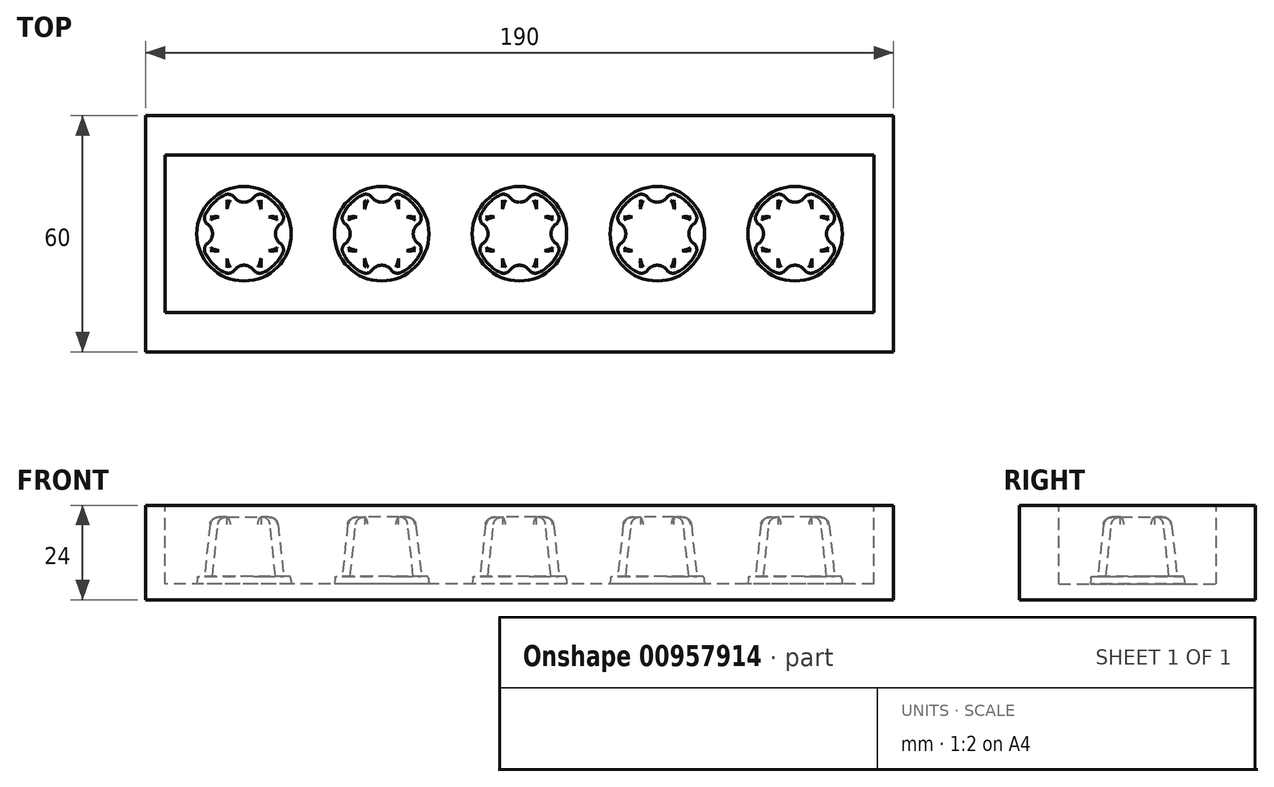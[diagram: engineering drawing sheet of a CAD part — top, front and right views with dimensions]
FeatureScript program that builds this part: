
annotation { "Feature Type Name" : "Feature", "Feature Type Description" : "" }
export const myFeature = defineFeature(function(context is Context, id is Id, definition is map)
    precondition{}
    {
        {
            var Q0;
            Q0=qCreatedBy(makeId("Top.planeOp"),FACE);
            var sketch = newSketch(context, id + "F0", { "sketchPlane" : qUnion([Q0])});
            skLineSegment(sketch, "E0.bottom", {"start": v(0, 0) * mm, "end": v(190, 0) * mm});
            skLineSegment(sketch, "E0.top", {"start": v(0, -60) * mm, "end": v(190, -60) * mm});
            skLineSegment(sketch, "E0.left", {"start": v(0, 0) * mm, "end": v(0, -60) * mm});
            skLineSegment(sketch, "E0.right", {"start": v(190, 0) * mm, "end": v(190, -60) * mm});
            skSolve(sketch);
        }
        {
            var Q0;
            Q0=makeQuery(id+"F0.imprint","IMPRINT",FACE,{"disambiguationData":[TD([[makeQuery(id+"F0.imprint","IMPRINT",EDGE,{"derivedFrom":sQuery(id+"F0.wireOp",EDGE,"E0.bottom")}),-1.0]])]});
            extrude(context, id + "F1", {"entities" : qUnion([Q0]), "depth" : 24 * mm, "offsetDistance" : 25 * mm});
        }
        {
            var Q0;
            Q0=makeQuery(id+"F1.opExtrude","CAP_FACE",FACE,{"disambiguationData":[OSD([sQuery(id+"F0.wireOp",EDGE,"E0.bottom"),sQuery(id+"F0.wireOp",EDGE,"E0.top"),sQuery(id+"F0.wireOp",EDGE,"E0.left"),sQuery(id+"F0.wireOp",EDGE,"E0.right")])],"isStart":false});
            var sketch = newSketch(context, id + "F2", { "sketchPlane" : qUnion([Q0])});
            skLineSegment(sketch, "E1.bottom", {"start": v(185, -50) * mm, "end": v(5, -50) * mm});
            skLineSegment(sketch, "E1.top", {"start": v(185, -10) * mm, "end": v(5, -10) * mm});
            skLineSegment(sketch, "E1.left", {"start": v(185, -50) * mm, "end": v(185, -10) * mm});
            skLineSegment(sketch, "E1.right", {"start": v(5, -50) * mm, "end": v(5, -10) * mm});
            skPoint(sketch, "E1.middle", {"position": v(95, -30) * mm});
            skPoint(sketch, "E1.middle.positionSnap0", {"position": v(0, -30) * mm});
            skPoint(sketch, "E1.middle.positionSnap1", {"position": v(95, 0) * mm});
            skPoint(sketch, "E1.centerSnap0", {"position": v(0, -30) * mm});
            skPoint(sketch, "E1.centerSnap1", {"position": v(95, 0) * mm});
            skSolve(sketch);
        }
        {
            var Q0;
            Q0=makeQuery(id+"F2.imprint","IMPRINT",FACE,{"disambiguationData":[TD([[makeQuery(id+"F2.imprint","IMPRINT",EDGE,{"derivedFrom":sQuery(id+"F2.wireOp",EDGE,"E1.bottom")}),-1.0]])]});
            extrude(context, id + "F3", {"entities" : qUnion([Q0]), "operationType" : NewBodyOperationType.REMOVE, "oppositeDirection" : true, "depth" : 20 * mm, "offsetDistance" : 25 * mm});
        }
        {
            var Q0;
            Q0=makeQuery(id+"F3.boolean.opBoolean","COPY",FACE,{"derivedFrom":makeQuery(id+"F3.opExtrude","CAP_FACE",FACE,{"disambiguationData":[OSD([sQuery(id+"F2.wireOp",EDGE,"E1.bottom"),sQuery(id+"F2.wireOp",EDGE,"E1.top"),sQuery(id+"F2.wireOp",EDGE,"E1.left"),sQuery(id+"F2.wireOp",EDGE,"E1.right")])],"isStart":false})});
            var sketch = newSketch(context, id + "F4", { "sketchPlane" : qUnion([Q0])});
            skLineSegment(sketch, "E2", {"start": v(5, -30) * mm, "end": v(185, -30) * mm, "construction": true});
            skCircle(sketch, "E3", {"center": v(25, -30) * mm, "radius": 12 * mm});
            skCircle(sketch, "E4.1.0.0", {"center": v(60, -30) * mm, "radius": 12 * mm});
            skCircle(sketch, "E4.2.0.0", {"center": v(95, -30) * mm, "radius": 12 * mm});
            skCircle(sketch, "E4.3.0.0", {"center": v(130, -30) * mm, "radius": 12 * mm});
            skCircle(sketch, "E4.4.0.0", {"center": v(165, -30) * mm, "radius": 12 * mm});
            skLineSegment(sketch, "E4.direction1", {"start": v(25, -30) * mm, "end": v(60, -30) * mm, "construction": true});
            skSolve(sketch);
        }
        {
            var Q0;
            Q0=makeQuery(id+"F4.imprint","IMPRINT",FACE,{"disambiguationData":[TD([[makeQuery(id+"F4.imprint","IMPRINT",EDGE,{"derivedFrom":sQuery(id+"F4.wireOp",EDGE,"E3")}),1.0]])]});
            var Q1;
            Q1=makeQuery(id+"F4.imprint","IMPRINT",FACE,{"disambiguationData":[TD([[makeQuery(id+"F4.imprint","IMPRINT",EDGE,{"derivedFrom":sQuery(id+"F4.wireOp",EDGE,"E4.1.0.0")}),1.0]])]});
            var Q2;
            Q2=makeQuery(id+"F4.imprint","IMPRINT",FACE,{"disambiguationData":[TD([[makeQuery(id+"F4.imprint","IMPRINT",EDGE,{"derivedFrom":sQuery(id+"F4.wireOp",EDGE,"E4.2.0.0")}),1.0]])]});
            var Q3;
            Q3=makeQuery(id+"F4.imprint","IMPRINT",FACE,{"disambiguationData":[TD([[makeQuery(id+"F4.imprint","IMPRINT",EDGE,{"derivedFrom":sQuery(id+"F4.wireOp",EDGE,"E4.3.0.0")}),1.0]])]});
            var Q4;
            Q4=makeQuery(id+"F4.imprint","IMPRINT",FACE,{"disambiguationData":[TD([[makeQuery(id+"F4.imprint","IMPRINT",EDGE,{"derivedFrom":sQuery(id+"F4.wireOp",EDGE,"E4.4.0.0")}),1.0]])]});
            extrude(context, id + "F5", {"entities" : qUnion([Q0, Q1, Q2, Q3, Q4]), "operationType" : NewBodyOperationType.ADD, "depth" : 2 * mm, "offsetDistance" : 25 * mm, "hasDraft" : true, "draftAngle" : 6 * degree, "draftPullDirection" : true});
        }
        {
            var Q0;
            Q0=makeQuery(id+"F5.opExtrude","CAP_FACE",FACE,{"disambiguationData":[OSD([sQuery(id+"F4.wireOp",EDGE,"E3")])],"isStart":false});
            var sketch = newSketch(context, id + "F6", { "sketchPlane" : qUnion([Q0])});
            skArc(sketch, "E5", {"start": v(20.07, -20.17) * mm, "mid": v(17.22, -22.22) * mm, "end": v(15.17, -25.07) * mm});
            skArc(sketch, "E6", {"start": v(22.58, -20.77) * mm, "mid": v(25, -22) * mm, "end": v(27.42, -20.77) * mm});
            skArc(sketch, "E7", {"start": v(34.23, -27.58) * mm, "mid": v(33, -30) * mm, "end": v(34.23, -32.42) * mm});
            skArc(sketch, "E8", {"start": v(27.42, -39.23) * mm, "mid": v(25, -38) * mm, "end": v(22.58, -39.23) * mm});
            skArc(sketch, "E9", {"start": v(15.77, -32.42) * mm, "mid": v(17, -30) * mm, "end": v(15.77, -27.58) * mm});
            skArc(sketch, "E10.trimOffspring", {"start": v(34.83, -25.07) * mm, "mid": v(32.78, -22.22) * mm, "end": v(29.93, -20.17) * mm});
            skArc(sketch, "E11.trimOffspring", {"start": v(29.93, -39.83) * mm, "mid": v(32.78, -37.78) * mm, "end": v(34.83, -34.93) * mm});
            skArc(sketch, "E12.trimOffspring", {"start": v(15.17, -34.93) * mm, "mid": v(17.22, -37.78) * mm, "end": v(20.07, -39.83) * mm});
            skPoint(sketch, "E13.visualSharp", {"position": v(22.03, -19.4) * mm});
            skArc(sketch, "E13.filletArc", {"start": v(22.58, -20.77) * mm, "mid": v(21.44, -20.01) * mm, "end": v(20.07, -20.17) * mm});
            skPoint(sketch, "E14.visualSharp", {"position": v(27.97, -19.4) * mm});
            skArc(sketch, "E14.filletArc", {"start": v(29.93, -20.17) * mm, "mid": v(28.56, -20.01) * mm, "end": v(27.42, -20.77) * mm});
            skPoint(sketch, "E15.visualSharp", {"position": v(35.6, -27.03) * mm});
            skArc(sketch, "E15.filletArc", {"start": v(34.23, -27.58) * mm, "mid": v(34.99, -26.44) * mm, "end": v(34.83, -25.07) * mm});
            skPoint(sketch, "E16.visualSharp", {"position": v(35.6, -32.97) * mm});
            skArc(sketch, "E16.filletArc", {"start": v(34.83, -34.93) * mm, "mid": v(34.99, -33.56) * mm, "end": v(34.23, -32.42) * mm});
            skPoint(sketch, "E17.visualSharp", {"position": v(27.97, -40.6) * mm});
            skArc(sketch, "E17.filletArc", {"start": v(27.42, -39.23) * mm, "mid": v(28.56, -39.99) * mm, "end": v(29.93, -39.83) * mm});
            skPoint(sketch, "E18.visualSharp", {"position": v(22.03, -40.6) * mm});
            skArc(sketch, "E18.filletArc", {"start": v(20.07, -39.83) * mm, "mid": v(21.44, -39.99) * mm, "end": v(22.58, -39.23) * mm});
            skPoint(sketch, "E19.visualSharp", {"position": v(14.4, -32.97) * mm});
            skArc(sketch, "E19.filletArc", {"start": v(15.77, -32.42) * mm, "mid": v(15.01, -33.56) * mm, "end": v(15.17, -34.93) * mm});
            skPoint(sketch, "E20.visualSharp", {"position": v(14.4, -27.03) * mm});
            skArc(sketch, "E20.filletArc", {"start": v(15.17, -25.07) * mm, "mid": v(15.01, -26.44) * mm, "end": v(15.77, -27.58) * mm});
            skPoint(sketch, "E21.1.0.0", {"position": v(70.6, -32.97) * mm});
            skPoint(sketch, "E21.1.0.1", {"position": v(62.97, -19.4) * mm});
            skArc(sketch, "E21.1.0.2", {"start": v(50.77, -32.42) * mm, "mid": v(52, -30) * mm, "end": v(50.77, -27.58) * mm});
            skPoint(sketch, "E21.1.0.3", {"position": v(70.6, -27.03) * mm});
            skArc(sketch, "E21.1.0.4", {"start": v(64.93, -39.83) * mm, "mid": v(67.78, -37.78) * mm, "end": v(69.83, -34.93) * mm});
            skPoint(sketch, "E21.1.0.5", {"position": v(57.03, -40.6) * mm});
            skPoint(sketch, "E21.1.0.6", {"position": v(57.03, -19.4) * mm});
            skArc(sketch, "E21.1.0.7", {"start": v(62.42, -39.23) * mm, "mid": v(60, -38) * mm, "end": v(57.58, -39.23) * mm});
            skPoint(sketch, "E21.1.0.8", {"position": v(49.4, -32.97) * mm});
            skArc(sketch, "E21.1.0.9", {"start": v(57.58, -20.77) * mm, "mid": v(60, -22) * mm, "end": v(62.42, -20.77) * mm});
            skArc(sketch, "E21.1.0.10", {"start": v(55.07, -20.17) * mm, "mid": v(52.22, -22.22) * mm, "end": v(50.17, -25.07) * mm});
            skArc(sketch, "E21.1.0.11", {"start": v(69.23, -27.58) * mm, "mid": v(68, -30) * mm, "end": v(69.23, -32.42) * mm});
            skArc(sketch, "E21.1.0.12", {"start": v(50.17, -34.93) * mm, "mid": v(52.22, -37.78) * mm, "end": v(55.07, -39.83) * mm});
            skPoint(sketch, "E21.1.0.13", {"position": v(62.97, -40.6) * mm});
            skArc(sketch, "E21.1.0.14", {"start": v(69.83, -25.07) * mm, "mid": v(67.78, -22.22) * mm, "end": v(64.93, -20.17) * mm});
            skPoint(sketch, "E21.1.0.15", {"position": v(49.4, -27.03) * mm});
            skArc(sketch, "E21.1.0.16", {"start": v(62.42, -39.23) * mm, "mid": v(63.56, -39.99) * mm, "end": v(64.93, -39.83) * mm});
            skArc(sketch, "E21.1.0.17", {"start": v(50.77, -32.42) * mm, "mid": v(50.01, -33.56) * mm, "end": v(50.17, -34.93) * mm});
            skArc(sketch, "E21.1.0.18", {"start": v(69.83, -34.93) * mm, "mid": v(69.99, -33.56) * mm, "end": v(69.23, -32.42) * mm});
            skArc(sketch, "E21.1.0.19", {"start": v(69.23, -27.58) * mm, "mid": v(69.99, -26.44) * mm, "end": v(69.83, -25.07) * mm});
            skArc(sketch, "E21.1.0.20", {"start": v(57.58, -20.77) * mm, "mid": v(56.44, -20.01) * mm, "end": v(55.07, -20.17) * mm});
            skArc(sketch, "E21.1.0.21", {"start": v(55.07, -39.83) * mm, "mid": v(56.44, -39.99) * mm, "end": v(57.58, -39.23) * mm});
            skArc(sketch, "E21.1.0.22", {"start": v(64.93, -20.17) * mm, "mid": v(63.56, -20.01) * mm, "end": v(62.42, -20.77) * mm});
            skArc(sketch, "E21.1.0.23", {"start": v(50.17, -25.07) * mm, "mid": v(50.01, -26.44) * mm, "end": v(50.77, -27.58) * mm});
            skPoint(sketch, "E21.2.0.0", {"position": v(105.6, -32.97) * mm});
            skPoint(sketch, "E21.2.0.1", {"position": v(97.97, -19.4) * mm});
            skArc(sketch, "E21.2.0.2", {"start": v(85.77, -32.42) * mm, "mid": v(87, -30) * mm, "end": v(85.77, -27.58) * mm});
            skPoint(sketch, "E21.2.0.3", {"position": v(105.6, -27.03) * mm});
            skArc(sketch, "E21.2.0.4", {"start": v(99.93, -39.83) * mm, "mid": v(102.78, -37.78) * mm, "end": v(104.83, -34.93) * mm});
            skPoint(sketch, "E21.2.0.5", {"position": v(92.03, -40.6) * mm});
            skPoint(sketch, "E21.2.0.6", {"position": v(92.03, -19.4) * mm});
            skArc(sketch, "E21.2.0.7", {"start": v(97.42, -39.23) * mm, "mid": v(95, -38) * mm, "end": v(92.58, -39.23) * mm});
            skPoint(sketch, "E21.2.0.8", {"position": v(84.4, -32.97) * mm});
            skArc(sketch, "E21.2.0.9", {"start": v(92.58, -20.77) * mm, "mid": v(95, -22) * mm, "end": v(97.42, -20.77) * mm});
            skArc(sketch, "E21.2.0.10", {"start": v(90.07, -20.17) * mm, "mid": v(87.22, -22.22) * mm, "end": v(85.17, -25.07) * mm});
            skArc(sketch, "E21.2.0.11", {"start": v(104.23, -27.58) * mm, "mid": v(103, -30) * mm, "end": v(104.23, -32.42) * mm});
            skArc(sketch, "E21.2.0.12", {"start": v(85.17, -34.93) * mm, "mid": v(87.22, -37.78) * mm, "end": v(90.07, -39.83) * mm});
            skPoint(sketch, "E21.2.0.13", {"position": v(97.97, -40.6) * mm});
            skArc(sketch, "E21.2.0.14", {"start": v(104.83, -25.07) * mm, "mid": v(102.78, -22.22) * mm, "end": v(99.93, -20.17) * mm});
            skPoint(sketch, "E21.2.0.15", {"position": v(84.4, -27.03) * mm});
            skArc(sketch, "E21.2.0.16", {"start": v(97.42, -39.23) * mm, "mid": v(98.56, -39.99) * mm, "end": v(99.93, -39.83) * mm});
            skArc(sketch, "E21.2.0.17", {"start": v(85.77, -32.42) * mm, "mid": v(85.01, -33.56) * mm, "end": v(85.17, -34.93) * mm});
            skArc(sketch, "E21.2.0.18", {"start": v(104.83, -34.93) * mm, "mid": v(104.99, -33.56) * mm, "end": v(104.23, -32.42) * mm});
            skArc(sketch, "E21.2.0.19", {"start": v(104.23, -27.58) * mm, "mid": v(104.99, -26.44) * mm, "end": v(104.83, -25.07) * mm});
            skArc(sketch, "E21.2.0.20", {"start": v(92.58, -20.77) * mm, "mid": v(91.44, -20.01) * mm, "end": v(90.07, -20.17) * mm});
            skArc(sketch, "E21.2.0.21", {"start": v(90.07, -39.83) * mm, "mid": v(91.44, -39.99) * mm, "end": v(92.58, -39.23) * mm});
            skArc(sketch, "E21.2.0.22", {"start": v(99.93, -20.17) * mm, "mid": v(98.56, -20.01) * mm, "end": v(97.42, -20.77) * mm});
            skArc(sketch, "E21.2.0.23", {"start": v(85.17, -25.07) * mm, "mid": v(85.01, -26.44) * mm, "end": v(85.77, -27.58) * mm});
            skPoint(sketch, "E21.3.0.0", {"position": v(140.6, -32.97) * mm});
            skPoint(sketch, "E21.3.0.1", {"position": v(132.97, -19.4) * mm});
            skArc(sketch, "E21.3.0.2", {"start": v(120.77, -32.42) * mm, "mid": v(122, -30) * mm, "end": v(120.77, -27.58) * mm});
            skPoint(sketch, "E21.3.0.3", {"position": v(140.6, -27.03) * mm});
            skArc(sketch, "E21.3.0.4", {"start": v(134.93, -39.83) * mm, "mid": v(137.78, -37.78) * mm, "end": v(139.83, -34.93) * mm});
            skPoint(sketch, "E21.3.0.5", {"position": v(127.03, -40.6) * mm});
            skPoint(sketch, "E21.3.0.6", {"position": v(127.03, -19.4) * mm});
            skArc(sketch, "E21.3.0.7", {"start": v(132.42, -39.23) * mm, "mid": v(130, -38) * mm, "end": v(127.58, -39.23) * mm});
            skPoint(sketch, "E21.3.0.8", {"position": v(119.4, -32.97) * mm});
            skArc(sketch, "E21.3.0.9", {"start": v(127.58, -20.77) * mm, "mid": v(130, -22) * mm, "end": v(132.42, -20.77) * mm});
            skArc(sketch, "E21.3.0.10", {"start": v(125.07, -20.17) * mm, "mid": v(122.22, -22.22) * mm, "end": v(120.17, -25.07) * mm});
            skArc(sketch, "E21.3.0.11", {"start": v(139.23, -27.58) * mm, "mid": v(138, -30) * mm, "end": v(139.23, -32.42) * mm});
            skArc(sketch, "E21.3.0.12", {"start": v(120.17, -34.93) * mm, "mid": v(122.22, -37.78) * mm, "end": v(125.07, -39.83) * mm});
            skPoint(sketch, "E21.3.0.13", {"position": v(132.97, -40.6) * mm});
            skArc(sketch, "E21.3.0.14", {"start": v(139.83, -25.07) * mm, "mid": v(137.78, -22.22) * mm, "end": v(134.93, -20.17) * mm});
            skPoint(sketch, "E21.3.0.15", {"position": v(119.4, -27.03) * mm});
            skArc(sketch, "E21.3.0.16", {"start": v(132.42, -39.23) * mm, "mid": v(133.56, -39.99) * mm, "end": v(134.93, -39.83) * mm});
            skArc(sketch, "E21.3.0.17", {"start": v(120.77, -32.42) * mm, "mid": v(120.01, -33.56) * mm, "end": v(120.17, -34.93) * mm});
            skArc(sketch, "E21.3.0.18", {"start": v(139.83, -34.93) * mm, "mid": v(139.99, -33.56) * mm, "end": v(139.23, -32.42) * mm});
            skArc(sketch, "E21.3.0.19", {"start": v(139.23, -27.58) * mm, "mid": v(139.99, -26.44) * mm, "end": v(139.83, -25.07) * mm});
            skArc(sketch, "E21.3.0.20", {"start": v(127.58, -20.77) * mm, "mid": v(126.44, -20.01) * mm, "end": v(125.07, -20.17) * mm});
            skArc(sketch, "E21.3.0.21", {"start": v(125.07, -39.83) * mm, "mid": v(126.44, -39.99) * mm, "end": v(127.58, -39.23) * mm});
            skArc(sketch, "E21.3.0.22", {"start": v(134.93, -20.17) * mm, "mid": v(133.56, -20.01) * mm, "end": v(132.42, -20.77) * mm});
            skArc(sketch, "E21.3.0.23", {"start": v(120.17, -25.07) * mm, "mid": v(120.01, -26.44) * mm, "end": v(120.77, -27.58) * mm});
            skPoint(sketch, "E21.4.0.0", {"position": v(175.6, -32.97) * mm});
            skPoint(sketch, "E21.4.0.1", {"position": v(167.97, -19.4) * mm});
            skArc(sketch, "E21.4.0.2", {"start": v(155.77, -32.42) * mm, "mid": v(157, -30) * mm, "end": v(155.77, -27.58) * mm});
            skPoint(sketch, "E21.4.0.3", {"position": v(175.6, -27.03) * mm});
            skArc(sketch, "E21.4.0.4", {"start": v(169.93, -39.83) * mm, "mid": v(172.78, -37.78) * mm, "end": v(174.83, -34.93) * mm});
            skPoint(sketch, "E21.4.0.5", {"position": v(162.03, -40.6) * mm});
            skPoint(sketch, "E21.4.0.6", {"position": v(162.03, -19.4) * mm});
            skArc(sketch, "E21.4.0.7", {"start": v(167.42, -39.23) * mm, "mid": v(165, -38) * mm, "end": v(162.58, -39.23) * mm});
            skPoint(sketch, "E21.4.0.8", {"position": v(154.4, -32.97) * mm});
            skArc(sketch, "E21.4.0.9", {"start": v(162.58, -20.77) * mm, "mid": v(165, -22) * mm, "end": v(167.42, -20.77) * mm});
            skArc(sketch, "E21.4.0.10", {"start": v(160.07, -20.17) * mm, "mid": v(157.22, -22.22) * mm, "end": v(155.17, -25.07) * mm});
            skArc(sketch, "E21.4.0.11", {"start": v(174.23, -27.58) * mm, "mid": v(173, -30) * mm, "end": v(174.23, -32.42) * mm});
            skArc(sketch, "E21.4.0.12", {"start": v(155.17, -34.93) * mm, "mid": v(157.22, -37.78) * mm, "end": v(160.07, -39.83) * mm});
            skPoint(sketch, "E21.4.0.13", {"position": v(167.97, -40.6) * mm});
            skArc(sketch, "E21.4.0.14", {"start": v(174.83, -25.07) * mm, "mid": v(172.78, -22.22) * mm, "end": v(169.93, -20.17) * mm});
            skPoint(sketch, "E21.4.0.15", {"position": v(154.4, -27.03) * mm});
            skArc(sketch, "E21.4.0.16", {"start": v(167.42, -39.23) * mm, "mid": v(168.56, -39.99) * mm, "end": v(169.93, -39.83) * mm});
            skArc(sketch, "E21.4.0.17", {"start": v(155.77, -32.42) * mm, "mid": v(155.01, -33.56) * mm, "end": v(155.17, -34.93) * mm});
            skArc(sketch, "E21.4.0.18", {"start": v(174.83, -34.93) * mm, "mid": v(174.99, -33.56) * mm, "end": v(174.23, -32.42) * mm});
            skArc(sketch, "E21.4.0.19", {"start": v(174.23, -27.58) * mm, "mid": v(174.99, -26.44) * mm, "end": v(174.83, -25.07) * mm});
            skArc(sketch, "E21.4.0.20", {"start": v(162.58, -20.77) * mm, "mid": v(161.44, -20.01) * mm, "end": v(160.07, -20.17) * mm});
            skArc(sketch, "E21.4.0.21", {"start": v(160.07, -39.83) * mm, "mid": v(161.44, -39.99) * mm, "end": v(162.58, -39.23) * mm});
            skArc(sketch, "E21.4.0.22", {"start": v(169.93, -20.17) * mm, "mid": v(168.56, -20.01) * mm, "end": v(167.42, -20.77) * mm});
            skArc(sketch, "E21.4.0.23", {"start": v(155.17, -25.07) * mm, "mid": v(155.01, -26.44) * mm, "end": v(155.77, -27.58) * mm});
            skLineSegment(sketch, "E21.direction1", {"start": v(20.07, -39.83) * mm, "end": v(55.07, -39.83) * mm, "construction": true});
            skSolve(sketch);
        }
        {
            var Q0;
            Q0=makeQuery(id+"F6.imprint","IMPRINT",FACE,{"disambiguationData":[TD([[makeQuery(id+"F6.imprint","IMPRINT",EDGE,{"derivedFrom":sQuery(id+"F6.wireOp",EDGE,"E5")}),1.0]])]});
            var Q1;
            Q1=makeQuery(id+"F6.imprint","IMPRINT",FACE,{"disambiguationData":[TD([[makeQuery(id+"F6.imprint","IMPRINT",EDGE,{"derivedFrom":sQuery(id+"F6.wireOp",EDGE,"E21.1.0.2")}),-1.0]])]});
            var Q2;
            Q2=makeQuery(id+"F6.imprint","IMPRINT",FACE,{"disambiguationData":[TD([[makeQuery(id+"F6.imprint","IMPRINT",EDGE,{"derivedFrom":sQuery(id+"F6.wireOp",EDGE,"E21.2.0.2")}),-1.0]])]});
            var Q3;
            Q3=makeQuery(id+"F6.imprint","IMPRINT",FACE,{"disambiguationData":[TD([[makeQuery(id+"F6.imprint","IMPRINT",EDGE,{"derivedFrom":sQuery(id+"F6.wireOp",EDGE,"E21.3.0.2")}),-1.0]])]});
            var Q4;
            Q4=makeQuery(id+"F6.imprint","IMPRINT",FACE,{"disambiguationData":[TD([[makeQuery(id+"F6.imprint","IMPRINT",EDGE,{"derivedFrom":sQuery(id+"F6.wireOp",EDGE,"E21.4.0.2")}),-1.0]])]});
            extrude(context, id + "F7", {"entities" : qUnion([Q0, Q1, Q2, Q3, Q4]), "operationType" : NewBodyOperationType.ADD, "depth" : 15 * mm, "offsetDistance" : 25 * mm, "hasDraft" : true, "draftAngle" : 6 * degree, "draftPullDirection" : true});
        }
        {
            var Q0;
            Q0=makeQuery(id+"F7.opExtrude","CAP_FACE",FACE,{"disambiguationData":[OSD([sQuery(id+"F6.wireOp",EDGE,"E5"),sQuery(id+"F6.wireOp",EDGE,"E6"),sQuery(id+"F6.wireOp",EDGE,"E7"),sQuery(id+"F6.wireOp",EDGE,"E8"),sQuery(id+"F6.wireOp",EDGE,"E9"),sQuery(id+"F6.wireOp",EDGE,"E10.trimOffspring"),sQuery(id+"F6.wireOp",EDGE,"E11.trimOffspring"),sQuery(id+"F6.wireOp",EDGE,"E12.trimOffspring"),sQuery(id+"F6.wireOp",EDGE,"E13.filletArc"),sQuery(id+"F6.wireOp",EDGE,"E14.filletArc"),sQuery(id+"F6.wireOp",EDGE,"E15.filletArc"),sQuery(id+"F6.wireOp",EDGE,"E16.filletArc"),sQuery(id+"F6.wireOp",EDGE,"E17.filletArc"),sQuery(id+"F6.wireOp",EDGE,"E18.filletArc"),sQuery(id+"F6.wireOp",EDGE,"E19.filletArc"),sQuery(id+"F6.wireOp",EDGE,"E20.filletArc")])],"isStart":false});
            var Q1;
            Q1=makeQuery(id+"F7.opExtrude","CAP_FACE",FACE,{"disambiguationData":[OSD([sQuery(id+"F6.wireOp",EDGE,"E21.1.0.2"),sQuery(id+"F6.wireOp",EDGE,"E21.1.0.4"),sQuery(id+"F6.wireOp",EDGE,"E21.1.0.7"),sQuery(id+"F6.wireOp",EDGE,"E21.1.0.9"),sQuery(id+"F6.wireOp",EDGE,"E21.1.0.10"),sQuery(id+"F6.wireOp",EDGE,"E21.1.0.11"),sQuery(id+"F6.wireOp",EDGE,"E21.1.0.12"),sQuery(id+"F6.wireOp",EDGE,"E21.1.0.14"),sQuery(id+"F6.wireOp",EDGE,"E21.1.0.16"),sQuery(id+"F6.wireOp",EDGE,"E21.1.0.17"),sQuery(id+"F6.wireOp",EDGE,"E21.1.0.18"),sQuery(id+"F6.wireOp",EDGE,"E21.1.0.19"),sQuery(id+"F6.wireOp",EDGE,"E21.1.0.20"),sQuery(id+"F6.wireOp",EDGE,"E21.1.0.21"),sQuery(id+"F6.wireOp",EDGE,"E21.1.0.22"),sQuery(id+"F6.wireOp",EDGE,"E21.1.0.23")])],"isStart":false});
            var Q2;
            Q2=makeQuery(id+"F7.opExtrude","CAP_FACE",FACE,{"disambiguationData":[OSD([sQuery(id+"F6.wireOp",EDGE,"E21.2.0.2"),sQuery(id+"F6.wireOp",EDGE,"E21.2.0.4"),sQuery(id+"F6.wireOp",EDGE,"E21.2.0.7"),sQuery(id+"F6.wireOp",EDGE,"E21.2.0.9"),sQuery(id+"F6.wireOp",EDGE,"E21.2.0.10"),sQuery(id+"F6.wireOp",EDGE,"E21.2.0.11"),sQuery(id+"F6.wireOp",EDGE,"E21.2.0.12"),sQuery(id+"F6.wireOp",EDGE,"E21.2.0.14"),sQuery(id+"F6.wireOp",EDGE,"E21.2.0.16"),sQuery(id+"F6.wireOp",EDGE,"E21.2.0.17"),sQuery(id+"F6.wireOp",EDGE,"E21.2.0.18"),sQuery(id+"F6.wireOp",EDGE,"E21.2.0.19"),sQuery(id+"F6.wireOp",EDGE,"E21.2.0.20"),sQuery(id+"F6.wireOp",EDGE,"E21.2.0.21"),sQuery(id+"F6.wireOp",EDGE,"E21.2.0.22"),sQuery(id+"F6.wireOp",EDGE,"E21.2.0.23")])],"isStart":false});
            var Q3;
            Q3=makeQuery(id+"F7.opExtrude","CAP_FACE",FACE,{"disambiguationData":[OSD([sQuery(id+"F6.wireOp",EDGE,"E21.3.0.2"),sQuery(id+"F6.wireOp",EDGE,"E21.3.0.4"),sQuery(id+"F6.wireOp",EDGE,"E21.3.0.7"),sQuery(id+"F6.wireOp",EDGE,"E21.3.0.9"),sQuery(id+"F6.wireOp",EDGE,"E21.3.0.10"),sQuery(id+"F6.wireOp",EDGE,"E21.3.0.11"),sQuery(id+"F6.wireOp",EDGE,"E21.3.0.12"),sQuery(id+"F6.wireOp",EDGE,"E21.3.0.14"),sQuery(id+"F6.wireOp",EDGE,"E21.3.0.16"),sQuery(id+"F6.wireOp",EDGE,"E21.3.0.17"),sQuery(id+"F6.wireOp",EDGE,"E21.3.0.18"),sQuery(id+"F6.wireOp",EDGE,"E21.3.0.19"),sQuery(id+"F6.wireOp",EDGE,"E21.3.0.20"),sQuery(id+"F6.wireOp",EDGE,"E21.3.0.21"),sQuery(id+"F6.wireOp",EDGE,"E21.3.0.22"),sQuery(id+"F6.wireOp",EDGE,"E21.3.0.23")])],"isStart":false});
            var Q4;
            Q4=makeQuery(id+"F7.opExtrude","CAP_FACE",FACE,{"disambiguationData":[OSD([sQuery(id+"F6.wireOp",EDGE,"E21.4.0.2"),sQuery(id+"F6.wireOp",EDGE,"E21.4.0.4"),sQuery(id+"F6.wireOp",EDGE,"E21.4.0.7"),sQuery(id+"F6.wireOp",EDGE,"E21.4.0.9"),sQuery(id+"F6.wireOp",EDGE,"E21.4.0.10"),sQuery(id+"F6.wireOp",EDGE,"E21.4.0.11"),sQuery(id+"F6.wireOp",EDGE,"E21.4.0.12"),sQuery(id+"F6.wireOp",EDGE,"E21.4.0.14"),sQuery(id+"F6.wireOp",EDGE,"E21.4.0.16"),sQuery(id+"F6.wireOp",EDGE,"E21.4.0.17"),sQuery(id+"F6.wireOp",EDGE,"E21.4.0.18"),sQuery(id+"F6.wireOp",EDGE,"E21.4.0.19"),sQuery(id+"F6.wireOp",EDGE,"E21.4.0.20"),sQuery(id+"F6.wireOp",EDGE,"E21.4.0.21"),sQuery(id+"F6.wireOp",EDGE,"E21.4.0.22"),sQuery(id+"F6.wireOp",EDGE,"E21.4.0.23")])],"isStart":false});
            fillet(context, id + "F8", {"entities" : qUnion([Q0, Q1, Q2, Q3, Q4]), "radius" : 2 * mm, "tangentPropagation" : true, "allowEdgeOverflow" : false});
        }
        {
            var Q0;
            Q0=makeQuery(id+"F5.opExtrude","CAP_EDGE",EDGE,{"disambiguationData":[OSD([sQuery(id+"F4.wireOp",EDGE,"E3")])],"isStart":false});
            var Q1;
            Q1=makeQuery(id+"F5.opExtrude","CAP_EDGE",EDGE,{"disambiguationData":[OSD([sQuery(id+"F4.wireOp",EDGE,"E4.1.0.0")])],"isStart":false});
            var Q2;
            Q2=makeQuery(id+"F5.opExtrude","CAP_EDGE",EDGE,{"disambiguationData":[OSD([sQuery(id+"F4.wireOp",EDGE,"E4.2.0.0")])],"isStart":false});
            var Q3;
            Q3=makeQuery(id+"F5.opExtrude","CAP_EDGE",EDGE,{"disambiguationData":[OSD([sQuery(id+"F4.wireOp",EDGE,"E4.3.0.0")])],"isStart":false});
            var Q4;
            Q4=makeQuery(id+"F5.opExtrude","CAP_EDGE",EDGE,{"disambiguationData":[OSD([sQuery(id+"F4.wireOp",EDGE,"E4.4.0.0")])],"isStart":false});
            fillet(context, id + "F9", {"entities" : qUnion([Q0, Q1, Q2, Q3, Q4]), "radius" : 0.5 * mm, "tangentPropagation" : true, "allowEdgeOverflow" : false});
        }
    });
